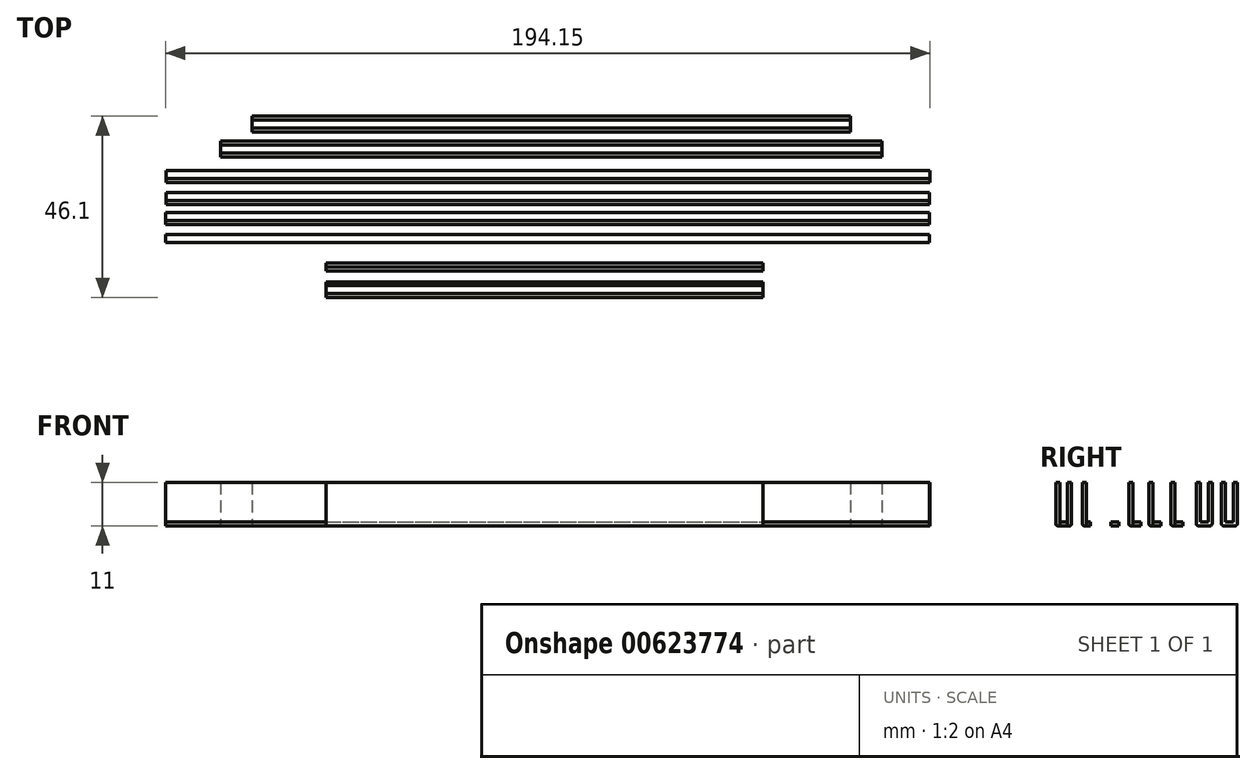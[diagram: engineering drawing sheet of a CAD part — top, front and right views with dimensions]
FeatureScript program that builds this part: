
annotation { "Feature Type Name" : "Feature", "Feature Type Description" : "" }
export const myFeature = defineFeature(function(context is Context, id is Id, definition is map)
    precondition{}
    {
        {
            var Q0;
            Q0=qCreatedBy(makeId("Top.planeOp"),FACE);
            var sketch = newSketch(context, id + "F0", { "sketchPlane" : qUnion([Q0])});
            skLineSegment(sketch, "E0.bottom", {"start": v(-57.22, 3.61) * mm, "end": v(53.78, 3.61) * mm});
            skLineSegment(sketch, "E0.top", {"start": v(-57.22, 2.61) * mm, "end": v(53.78, 2.61) * mm});
            skLineSegment(sketch, "E0.left", {"start": v(-57.22, 3.61) * mm, "end": v(-57.22, 2.61) * mm});
            skLineSegment(sketch, "E0.right", {"start": v(53.78, 3.61) * mm, "end": v(53.78, 2.61) * mm});
            skLineSegment(sketch, "E1.top", {"start": v(-57.22, 4.61) * mm, "end": v(53.78, 4.61) * mm});
            skLineSegment(sketch, "E1.left", {"start": v(-57.22, 3.61) * mm, "end": v(-57.22, 4.61) * mm});
            skLineSegment(sketch, "E1.right", {"start": v(53.78, 3.61) * mm, "end": v(53.78, 4.61) * mm});
            skLineSegment(sketch, "E2.top", {"start": v(-57.22, 1.61) * mm, "end": v(53.78, 1.61) * mm});
            skLineSegment(sketch, "E2.left", {"start": v(-57.22, 2.61) * mm, "end": v(-57.22, 1.61) * mm});
            skLineSegment(sketch, "E2.right", {"start": v(53.78, 2.61) * mm, "end": v(53.78, 1.61) * mm});
            skLineSegment(sketch, "E3.bottom", {"start": v(-57.22, -1.15) * mm, "end": v(53.78, -1.15) * mm});
            skLineSegment(sketch, "E3.top", {"start": v(-57.22, -2.15) * mm, "end": v(53.78, -2.15) * mm});
            skLineSegment(sketch, "E3.left", {"start": v(-57.22, -1.15) * mm, "end": v(-57.22, -2.15) * mm});
            skLineSegment(sketch, "E3.right", {"start": v(53.78, -1.15) * mm, "end": v(53.78, -2.15) * mm});
            skLineSegment(sketch, "E4.top", {"start": v(-57.22, -4.15) * mm, "end": v(53.78, -4.15) * mm});
            skLineSegment(sketch, "E4.left", {"start": v(-57.22, -2.15) * mm, "end": v(-57.22, -4.15) * mm});
            skLineSegment(sketch, "E4.right", {"start": v(53.78, -2.15) * mm, "end": v(53.78, -4.15) * mm});
            skLineSegment(sketch, "E5.top", {"start": v(-57.22, -5.15) * mm, "end": v(53.78, -5.15) * mm});
            skLineSegment(sketch, "E5.left", {"start": v(-57.22, -4.15) * mm, "end": v(-57.22, -5.15) * mm});
            skLineSegment(sketch, "E5.right", {"start": v(53.78, -4.15) * mm, "end": v(53.78, -5.15) * mm});
            skSolve(sketch);
        }
        {
            var Q0;
            Q0=makeQuery(id+"F0.imprint","IMPRINT",FACE,{"disambiguationData":[TD([[makeQuery(id+"F0.imprint","IMPRINT",EDGE,{"derivedFrom":sQuery(id+"F0.wireOp",EDGE,"E0.left")}),1.0]])]});
            var Q1;
            Q1=makeQuery(id+"F0.imprint","IMPRINT",FACE,{"disambiguationData":[TD([[makeQuery(id+"F0.imprint","IMPRINT",EDGE,{"derivedFrom":sQuery(id+"F0.wireOp",EDGE,"E3.top")}),-1.0]])]});
            extrude(context, id + "F1", {"entities" : qUnion([Q0, Q1]), "depth" : 1 * mm, "offsetDistance" : 25 * mm});
        }
        {
            var Q0;
            Q0=makeQuery(id+"F0.imprint","IMPRINT",FACE,{"disambiguationData":[TD([[makeQuery(id+"F0.imprint","IMPRINT",EDGE,{"derivedFrom":sQuery(id+"F0.wireOp",EDGE,"E0.bottom")}),1.0]])]});
            var Q1;
            Q1=makeQuery(id+"F0.imprint","IMPRINT",FACE,{"disambiguationData":[TD([[makeQuery(id+"F0.imprint","IMPRINT",EDGE,{"derivedFrom":sQuery(id+"F0.wireOp",EDGE,"E0.top")}),-1.0]])]});
            var Q2;
            Q2=makeQuery(id+"F0.imprint","IMPRINT",FACE,{"disambiguationData":[TD([[makeQuery(id+"F0.imprint","IMPRINT",EDGE,{"derivedFrom":sQuery(id+"F0.wireOp",EDGE,"E3.bottom")}),-1.0]])]});
            var Q3;
            Q3=makeQuery(id+"F0.imprint","IMPRINT",FACE,{"disambiguationData":[TD([[makeQuery(id+"F0.imprint","IMPRINT",EDGE,{"derivedFrom":sQuery(id+"F0.wireOp",EDGE,"E4.top")}),-1.0]])]});
            extrude(context, id + "F2", {"entities" : qUnion([Q0, Q1, Q2, Q3]), "depth" : 11 * mm, "offsetDistance" : 25 * mm});
        }
        {
            var Q0;
            Q0=makeQuery(id+"F2.opExtrude","CAP_EDGE",EDGE,{"disambiguationData":[OSD([sQuery(id+"F0.wireOp",EDGE,"E5.top")])],"isStart":true});
            var Q1;
            Q1=makeQuery(id+"F2.opExtrude","CAP_EDGE",EDGE,{"disambiguationData":[OSD([sQuery(id+"F0.wireOp",EDGE,"E3.bottom")])],"isStart":true});
            var Q2;
            Q2=makeQuery(id+"F2.opExtrude","CAP_EDGE",EDGE,{"disambiguationData":[OSD([sQuery(id+"F0.wireOp",EDGE,"E2.top")])],"isStart":true});
            var Q3;
            Q3=makeQuery(id+"F2.opExtrude","CAP_EDGE",EDGE,{"disambiguationData":[OSD([sQuery(id+"F0.wireOp",EDGE,"E1.top")])],"isStart":true});
            fillet(context, id + "F3", {"entities" : qUnion([Q0, Q1, Q2, Q3]), "radius" : .5 * mm, "tangentPropagation" : true, "allowEdgeOverflow" : false});
        }
        {
            var Q0;
            Q0=qCreatedBy(makeId("Top.planeOp"),FACE);
            var sketch = newSketch(context, id + "F4", { "sketchPlane" : qUnion([Q0])});
            skLineSegment(sketch, "E6.bottom", {"start": v(-97.95, 16.4) * mm, "end": v(96.05, 16.4) * mm});
            skLineSegment(sketch, "E6.top", {"start": v(-97.95, 14.4) * mm, "end": v(96.05, 14.4) * mm});
            skLineSegment(sketch, "E6.left", {"start": v(-97.95, 16.4) * mm, "end": v(-97.95, 14.4) * mm});
            skLineSegment(sketch, "E6.right", {"start": v(96.05, 16.4) * mm, "end": v(96.05, 14.4) * mm});
            skLineSegment(sketch, "E7.bottom", {"start": v(96.05, 16.4) * mm, "end": v(-97.95, 16.4) * mm});
            skLineSegment(sketch, "E7.top", {"start": v(96.05, 17.4) * mm, "end": v(-97.95, 17.4) * mm});
            skLineSegment(sketch, "E7.left", {"start": v(96.05, 16.4) * mm, "end": v(96.05, 17.4) * mm});
            skLineSegment(sketch, "E7.right", {"start": v(-97.95, 16.4) * mm, "end": v(-97.95, 17.4) * mm});
            skLineSegment(sketch, "E8.top", {"start": v(-97.95, 13.4) * mm, "end": v(96.05, 13.4) * mm});
            skLineSegment(sketch, "E8.left", {"start": v(-97.95, 14.4) * mm, "end": v(-97.95, 13.4) * mm});
            skLineSegment(sketch, "E8.right", {"start": v(96.05, 14.4) * mm, "end": v(96.05, 13.4) * mm});
            skLineSegment(sketch, "E9.bottom", {"start": v(-97.95, 10.83) * mm, "end": v(96.05, 10.83) * mm});
            skLineSegment(sketch, "E9.top", {"start": v(-97.95, 8.83) * mm, "end": v(96.05, 8.83) * mm});
            skLineSegment(sketch, "E9.left", {"start": v(-97.95, 10.83) * mm, "end": v(-97.95, 8.83) * mm});
            skLineSegment(sketch, "E9.right", {"start": v(96.05, 10.83) * mm, "end": v(96.05, 8.83) * mm});
            skLineSegment(sketch, "E10.bottom", {"start": v(96.05, 10.83) * mm, "end": v(-97.95, 10.83) * mm});
            skLineSegment(sketch, "E10.top", {"start": v(96.05, 11.83) * mm, "end": v(-97.95, 11.83) * mm});
            skLineSegment(sketch, "E10.left", {"start": v(96.05, 10.83) * mm, "end": v(96.05, 11.83) * mm});
            skLineSegment(sketch, "E10.right", {"start": v(-97.95, 10.83) * mm, "end": v(-97.95, 11.83) * mm});
            skLineSegment(sketch, "E11.top", {"start": v(-97.95, 7.83) * mm, "end": v(96.05, 7.83) * mm});
            skLineSegment(sketch, "E11.left", {"start": v(-97.95, 8.83) * mm, "end": v(-97.95, 7.83) * mm});
            skLineSegment(sketch, "E11.right", {"start": v(96.05, 8.83) * mm, "end": v(96.05, 7.83) * mm});
            skLineSegment(sketch, "E12.bottom", {"start": v(-97.8, 27.06) * mm, "end": v(96.2, 27.06) * mm});
            skLineSegment(sketch, "E12.top", {"start": v(-97.8, 25.06) * mm, "end": v(96.2, 25.06) * mm});
            skLineSegment(sketch, "E12.left", {"start": v(-97.8, 27.06) * mm, "end": v(-97.8, 25.06) * mm});
            skLineSegment(sketch, "E12.right", {"start": v(96.2, 27.06) * mm, "end": v(96.2, 25.06) * mm});
            skLineSegment(sketch, "E13.bottom", {"start": v(96.2, 27.06) * mm, "end": v(-97.8, 27.06) * mm});
            skLineSegment(sketch, "E13.top", {"start": v(96.2, 28.06) * mm, "end": v(-97.8, 28.06) * mm});
            skLineSegment(sketch, "E13.left", {"start": v(96.2, 27.06) * mm, "end": v(96.2, 28.06) * mm});
            skLineSegment(sketch, "E13.right", {"start": v(-97.8, 27.06) * mm, "end": v(-97.8, 28.06) * mm});
            skLineSegment(sketch, "E14.top", {"start": v(-97.8, 24.06) * mm, "end": v(96.2, 24.06) * mm});
            skLineSegment(sketch, "E14.left", {"start": v(-97.8, 25.06) * mm, "end": v(-97.8, 24.06) * mm});
            skLineSegment(sketch, "E14.right", {"start": v(96.2, 25.06) * mm, "end": v(96.2, 24.06) * mm});
            skLineSegment(sketch, "E15.bottom", {"start": v(-97.87, 21.5) * mm, "end": v(96.13, 21.5) * mm});
            skLineSegment(sketch, "E15.top", {"start": v(-97.87, 19.5) * mm, "end": v(96.13, 19.5) * mm});
            skLineSegment(sketch, "E15.left", {"start": v(-97.87, 21.5) * mm, "end": v(-97.87, 19.5) * mm});
            skLineSegment(sketch, "E15.right", {"start": v(96.13, 21.5) * mm, "end": v(96.13, 19.5) * mm});
            skLineSegment(sketch, "E16.bottom", {"start": v(96.13, 21.5) * mm, "end": v(-97.87, 21.5) * mm});
            skLineSegment(sketch, "E16.top", {"start": v(96.13, 22.5) * mm, "end": v(-97.87, 22.5) * mm});
            skLineSegment(sketch, "E16.left", {"start": v(96.13, 21.5) * mm, "end": v(96.13, 22.5) * mm});
            skLineSegment(sketch, "E16.right", {"start": v(-97.87, 21.5) * mm, "end": v(-97.87, 22.5) * mm});
            skLineSegment(sketch, "E17.top", {"start": v(-97.87, 18.5) * mm, "end": v(96.13, 18.5) * mm});
            skLineSegment(sketch, "E17.left", {"start": v(-97.87, 19.5) * mm, "end": v(-97.87, 18.5) * mm});
            skLineSegment(sketch, "E17.right", {"start": v(96.13, 19.5) * mm, "end": v(96.13, 18.5) * mm});
            skSolve(sketch);
        }
        {
            var Q0;
            Q0=makeQuery(id+"F4.imprint","IMPRINT",FACE,{"disambiguationData":[TD([[makeQuery(id+"F4.imprint","IMPRINT",EDGE,{"derivedFrom":sQuery(id+"F4.wireOp",EDGE,"E12.left")}),1.0]])]});
            var Q1;
            Q1=makeQuery(id+"F4.imprint","IMPRINT",FACE,{"disambiguationData":[TD([[makeQuery(id+"F4.imprint","IMPRINT",EDGE,{"derivedFrom":sQuery(id+"F4.wireOp",EDGE,"E15.left")}),1.0]])]});
            var Q2;
            Q2=makeQuery(id+"F4.imprint","IMPRINT",FACE,{"disambiguationData":[TD([[makeQuery(id+"F4.imprint","IMPRINT",EDGE,{"derivedFrom":sQuery(id+"F4.wireOp",EDGE,"E6.left")}),1.0]])]});
            var Q3;
            Q3=makeQuery(id+"F4.imprint","IMPRINT",FACE,{"disambiguationData":[TD([[makeQuery(id+"F4.imprint","IMPRINT",EDGE,{"derivedFrom":sQuery(id+"F4.wireOp",EDGE,"E9.left")}),1.0]])]});
            extrude(context, id + "F5", {"entities" : qUnion([Q0, Q1, Q2, Q3]), "depth" : 1 * mm, "offsetDistance" : 25 * mm});
        }
        {
            var Q0;
            Q0=makeQuery(id+"F4.imprint","IMPRINT",FACE,{"disambiguationData":[TD([[makeQuery(id+"F4.imprint","IMPRINT",EDGE,{"derivedFrom":sQuery(id+"F4.wireOp",EDGE,"E13.bottom")}),-1.0]])]});
            var Q1;
            Q1=makeQuery(id+"F4.imprint","IMPRINT",FACE,{"disambiguationData":[TD([[makeQuery(id+"F4.imprint","IMPRINT",EDGE,{"derivedFrom":sQuery(id+"F4.wireOp",EDGE,"E12.top")}),-1.0]])]});
            var Q2;
            Q2=makeQuery(id+"F4.imprint","IMPRINT",FACE,{"disambiguationData":[TD([[makeQuery(id+"F4.imprint","IMPRINT",EDGE,{"derivedFrom":sQuery(id+"F4.wireOp",EDGE,"E16.bottom")}),-1.0]])]});
            var Q3;
            Q3=makeQuery(id+"F4.imprint","IMPRINT",FACE,{"disambiguationData":[TD([[makeQuery(id+"F4.imprint","IMPRINT",EDGE,{"derivedFrom":sQuery(id+"F4.wireOp",EDGE,"E15.top")}),-1.0]])]});
            var Q4;
            Q4=makeQuery(id+"F4.imprint","IMPRINT",FACE,{"disambiguationData":[TD([[makeQuery(id+"F4.imprint","IMPRINT",EDGE,{"derivedFrom":sQuery(id+"F4.wireOp",EDGE,"E7.bottom")}),-1.0]])]});
            var Q5;
            Q5=makeQuery(id+"F4.imprint","IMPRINT",FACE,{"disambiguationData":[TD([[makeQuery(id+"F4.imprint","IMPRINT",EDGE,{"derivedFrom":sQuery(id+"F4.wireOp",EDGE,"E6.top")}),-1.0]])]});
            var Q6;
            Q6=makeQuery(id+"F4.imprint","IMPRINT",FACE,{"disambiguationData":[TD([[makeQuery(id+"F4.imprint","IMPRINT",EDGE,{"derivedFrom":sQuery(id+"F4.wireOp",EDGE,"E10.bottom")}),-1.0]])]});
            var Q7;
            Q7=makeQuery(id+"F4.imprint","IMPRINT",FACE,{"disambiguationData":[TD([[makeQuery(id+"F4.imprint","IMPRINT",EDGE,{"derivedFrom":sQuery(id+"F4.wireOp",EDGE,"E9.top")}),-1.0]])]});
            extrude(context, id + "F6", {"entities" : qUnion([Q0, Q1, Q2, Q3, Q4, Q5, Q6, Q7]), "depth" : 11 * mm, "offsetDistance" : 25 * mm});
        }
        {
            var Q0;
            Q0=makeQuery(id+"F6.opExtrude","CAP_EDGE",EDGE,{"disambiguationData":[OSD([sQuery(id+"F4.wireOp",EDGE,"E11.top")])],"isStart":true});
            var Q1;
            Q1=makeQuery(id+"F6.opExtrude","CAP_EDGE",EDGE,{"disambiguationData":[OSD([sQuery(id+"F4.wireOp",EDGE,"E10.top")])],"isStart":true});
            var Q2;
            Q2=makeQuery(id+"F6.opExtrude","CAP_EDGE",EDGE,{"disambiguationData":[OSD([sQuery(id+"F4.wireOp",EDGE,"E8.top")])],"isStart":true});
            var Q3;
            Q3=makeQuery(id+"F6.opExtrude","CAP_EDGE",EDGE,{"disambiguationData":[OSD([sQuery(id+"F4.wireOp",EDGE,"E7.top")])],"isStart":true});
            var Q4;
            Q4=makeQuery(id+"F6.opExtrude","CAP_EDGE",EDGE,{"disambiguationData":[OSD([sQuery(id+"F4.wireOp",EDGE,"E17.top")])],"isStart":true});
            var Q5;
            Q5=makeQuery(id+"F6.opExtrude","CAP_EDGE",EDGE,{"disambiguationData":[OSD([sQuery(id+"F4.wireOp",EDGE,"E16.top")])],"isStart":true});
            var Q6;
            Q6=makeQuery(id+"F6.opExtrude","CAP_EDGE",EDGE,{"disambiguationData":[OSD([sQuery(id+"F4.wireOp",EDGE,"E14.top")])],"isStart":true});
            var Q7;
            Q7=makeQuery(id+"F6.opExtrude","CAP_EDGE",EDGE,{"disambiguationData":[OSD([sQuery(id+"F4.wireOp",EDGE,"E13.top")])],"isStart":true});
            fillet(context, id + "F7", {"entities" : qUnion([Q0, Q1, Q2, Q3, Q4, Q5, Q6, Q7]), "radius" : .5 * mm, "tangentPropagation" : true, "allowEdgeOverflow" : false});
        }
        {
            var Q0;
            Q0=qCreatedBy(makeId("Top.planeOp"),FACE);
            var sketch = newSketch(context, id + "F8", { "sketchPlane" : qUnion([Q0])});
            skLineSegment(sketch, "E18.bottom", {"start": v(-84, 33.56) * mm, "end": v(84, 33.56) * mm});
            skLineSegment(sketch, "E18.top", {"start": v(-84, 31.56) * mm, "end": v(84, 31.56) * mm});
            skLineSegment(sketch, "E18.left", {"start": v(-84, 33.56) * mm, "end": v(-84, 31.56) * mm});
            skLineSegment(sketch, "E18.right", {"start": v(84, 33.56) * mm, "end": v(84, 31.56) * mm});
            skPoint(sketch, "E18.middle", {"position": v(0, 32.56) * mm});
            skLineSegment(sketch, "E19.top", {"start": v(-84, 30.56) * mm, "end": v(84, 30.56) * mm});
            skLineSegment(sketch, "E19.left", {"start": v(-84, 31.56) * mm, "end": v(-84, 30.56) * mm});
            skLineSegment(sketch, "E19.right", {"start": v(84, 31.56) * mm, "end": v(84, 30.56) * mm});
            skLineSegment(sketch, "E20.top", {"start": v(-84, 34.56) * mm, "end": v(84, 34.56) * mm});
            skLineSegment(sketch, "E20.left", {"start": v(-84, 33.56) * mm, "end": v(-84, 34.56) * mm});
            skLineSegment(sketch, "E20.right", {"start": v(84, 33.56) * mm, "end": v(84, 34.56) * mm});
            skSolve(sketch);
        }
        {
            var Q0;
            Q0=makeQuery(id+"F8.imprint","IMPRINT",FACE,{"disambiguationData":[TD([[makeQuery(id+"F8.imprint","IMPRINT",EDGE,{"derivedFrom":sQuery(id+"F8.wireOp",EDGE,"E18.left")}),1.0]])]});
            extrude(context, id + "F9", {"entities" : qUnion([Q0]), "depth" : 1 * mm, "offsetDistance" : 25 * mm});
        }
        {
            var Q0;
            Q0=makeQuery(id+"F8.imprint","IMPRINT",FACE,{"disambiguationData":[TD([[makeQuery(id+"F8.imprint","IMPRINT",EDGE,{"derivedFrom":sQuery(id+"F8.wireOp",EDGE,"E18.bottom")}),1.0]])]});
            var Q1;
            Q1=makeQuery(id+"F8.imprint","IMPRINT",FACE,{"disambiguationData":[TD([[makeQuery(id+"F8.imprint","IMPRINT",EDGE,{"derivedFrom":sQuery(id+"F8.wireOp",EDGE,"E18.top")}),-1.0]])]});
            extrude(context, id + "F10", {"entities" : qUnion([Q0, Q1]), "operationType" : NewBodyOperationType.ADD, "depth" : 11 * mm, "offsetDistance" : 25 * mm});
        }
        {
            var Q0;
            Q0=makeQuery(id+"F10.opExtrude","CAP_EDGE",EDGE,{"disambiguationData":[OSD([sQuery(id+"F8.wireOp",EDGE,"E19.top")])],"isStart":true});
            var Q1;
            Q1=makeQuery(id+"F10.opExtrude","CAP_EDGE",EDGE,{"disambiguationData":[OSD([sQuery(id+"F8.wireOp",EDGE,"E20.top")])],"isStart":true});
            fillet(context, id + "F11", {"entities" : qUnion([Q0, Q1]), "radius" : .5 * mm, "tangentPropagation" : true, "allowEdgeOverflow" : false});
        }
        {
            var Q0;
            Q0=qCreatedBy(makeId("Top.planeOp"),FACE);
            var sketch = newSketch(context, id + "F12", { "sketchPlane" : qUnion([Q0])});
            skLineSegment(sketch, "E21.bottom", {"start": v(-76, 39.95) * mm, "end": v(76, 39.95) * mm});
            skLineSegment(sketch, "E21.top", {"start": v(-76, 37.95) * mm, "end": v(76, 37.95) * mm});
            skLineSegment(sketch, "E21.left", {"start": v(-76, 39.95) * mm, "end": v(-76, 37.95) * mm});
            skLineSegment(sketch, "E21.right", {"start": v(76, 39.95) * mm, "end": v(76, 37.95) * mm});
            skPoint(sketch, "E21.middle", {"position": v(0, 38.95) * mm});
            skLineSegment(sketch, "E22.top", {"start": v(-76, 40.95) * mm, "end": v(76, 40.95) * mm});
            skLineSegment(sketch, "E22.left", {"start": v(-76, 39.95) * mm, "end": v(-76, 40.95) * mm});
            skLineSegment(sketch, "E22.right", {"start": v(76, 39.95) * mm, "end": v(76, 40.95) * mm});
            skLineSegment(sketch, "E23.top", {"start": v(-76, 36.95) * mm, "end": v(76, 36.95) * mm});
            skLineSegment(sketch, "E23.left", {"start": v(-76, 37.95) * mm, "end": v(-76, 36.95) * mm});
            skLineSegment(sketch, "E23.right", {"start": v(76, 37.95) * mm, "end": v(76, 36.95) * mm});
            skSolve(sketch);
        }
        {
            var Q0;
            Q0=makeQuery(id+"F12.imprint","IMPRINT",FACE,{"disambiguationData":[TD([[makeQuery(id+"F12.imprint","IMPRINT",EDGE,{"derivedFrom":sQuery(id+"F12.wireOp",EDGE,"E21.left")}),1.0]])]});
            extrude(context, id + "F13", {"entities" : qUnion([Q0]), "depth" : 1 * mm, "offsetDistance" : 25 * mm});
        }
        {
            var Q0;
            Q0=makeQuery(id+"F12.imprint","IMPRINT",FACE,{"disambiguationData":[TD([[makeQuery(id+"F12.imprint","IMPRINT",EDGE,{"derivedFrom":sQuery(id+"F12.wireOp",EDGE,"E21.bottom")}),1.0]])]});
            var Q1;
            Q1=makeQuery(id+"F12.imprint","IMPRINT",FACE,{"disambiguationData":[TD([[makeQuery(id+"F12.imprint","IMPRINT",EDGE,{"derivedFrom":sQuery(id+"F12.wireOp",EDGE,"E21.top")}),-1.0]])]});
            extrude(context, id + "F14", {"entities" : qUnion([Q0, Q1]), "operationType" : NewBodyOperationType.ADD, "depth" : 11 * mm, "offsetDistance" : 25 * mm});
        }
        {
            var Q0;
            Q0=makeQuery(id+"F14.opExtrude","CAP_EDGE",EDGE,{"disambiguationData":[OSD([sQuery(id+"F12.wireOp",EDGE,"E22.top")])],"isStart":true});
            var Q1;
            Q1=makeQuery(id+"F14.opExtrude","CAP_EDGE",EDGE,{"disambiguationData":[OSD([sQuery(id+"F12.wireOp",EDGE,"E23.top")])],"isStart":true});
            fillet(context, id + "F15", {"entities" : qUnion([Q0, Q1]), "radius" : .5 * mm, "tangentPropagation" : true, "allowEdgeOverflow" : false});
        }
    });
